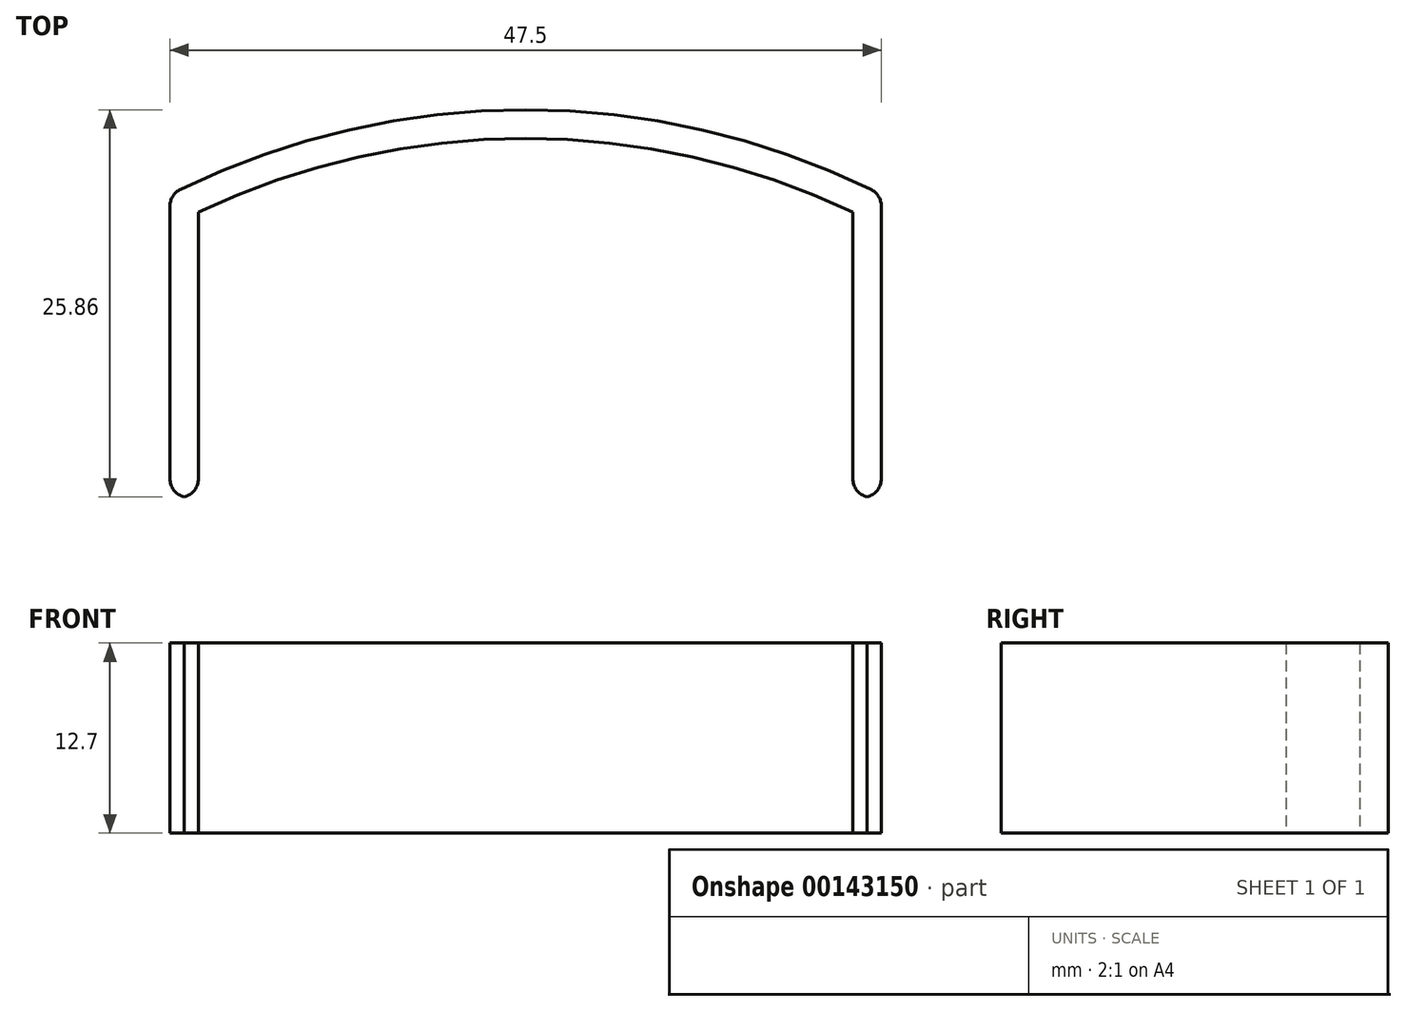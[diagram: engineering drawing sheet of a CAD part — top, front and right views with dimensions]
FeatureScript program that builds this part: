
annotation { "Feature Type Name" : "Feature", "Feature Type Description" : "" }
export const myFeature = defineFeature(function(context is Context, id is Id, definition is map)
    precondition{}
    {
        {
            var Q0;
            Q0=qCreatedBy(makeId("Top.planeOp"),FACE);
            var sketch = newSketch(context, id + "F0", { "sketchPlane" : qUnion([Q0])});
            skCircle(sketch, "E0", {"center": v(0, 0) * mm, "radius": 50.8 * mm});
            skCircle(sketch, "E1.0", {"center": v(0, 0) * mm, "radius": 52.7 * mm});
            skPoint(sketch, "E2", {"position": v(-21.84, 45.86) * mm});
            skPoint(sketch, "E3", {"position": v(-25.97, 45.86) * mm});
            skPoint(sketch, "E4", {"position": v(21.84, 45.86) * mm});
            skPoint(sketch, "E5", {"position": v(25.97, 45.86) * mm});
            skLineSegment(sketch, "E6", {"start": v(-25.97, 65.39) * mm, "end": v(-25.97, 26.81) * mm});
            skLineSegment(sketch, "E7", {"start": v(-21.84, 65.39) * mm, "end": v(-21.84, 26.81) * mm});
            skLineSegment(sketch, "E8", {"start": v(21.84, 65.39) * mm, "end": v(21.84, 26.81) * mm});
            skLineSegment(sketch, "E9", {"start": v(25.97, 65.39) * mm, "end": v(25.97, 26.81) * mm});
            skLineSegment(sketch, "E10", {"start": v(-25.97, 26.81) * mm, "end": v(-21.84, 26.81) * mm});
            skLineSegment(sketch, "E11", {"start": v(21.84, 26.81) * mm, "end": v(25.97, 26.81) * mm});
            skSolve(sketch);
        }
        {
            var Q0;
            {var subQ0=sQuery(id+"F0.wireOp",EDGE,"E7");var subQ1=sQuery(id+"F0.wireOp",EDGE,"E0");var subQ2=makeQuery(id+"F0.imprint","INTERSECT",VERTEX,{"derivedFrom":[subQ1,subQ0]});Q0=makeQuery(id+"F0.imprint","IMPRINT",FACE,{"disambiguationData":[TD([[makeQuery(id+"F0.imprint","IMPRINT",EDGE,{"disambiguationData":[TD([[subQ2,-1.0]])],"derivedFrom":subQ1}),-1.0]])]});}
            var Q1;
            {var subQ5=sQuery(id+"F0.wireOp",EDGE,"E10");Q1=makeQuery(id+"F0.imprint","IMPRINT",FACE,{"disambiguationData":[TD([[makeQuery(id+"F0.imprint","IMPRINT",EDGE,{"derivedFrom":subQ5}),1.0]])]});}
            var Q2;
            {var subQ0=sQuery(id+"F0.wireOp",EDGE,"E8");var subQ1=sQuery(id+"F0.wireOp",EDGE,"E0");var subQ2=makeQuery(id+"F0.imprint","INTERSECT",VERTEX,{"derivedFrom":[subQ1,subQ0]});Q2=makeQuery(id+"F0.imprint","IMPRINT",FACE,{"disambiguationData":[TD([[makeQuery(id+"F0.imprint","IMPRINT",EDGE,{"disambiguationData":[TD([[subQ2,1.0]])],"derivedFrom":subQ1}),-1.0]])]});}
            var Q3;
            {var subQ5=sQuery(id+"F0.wireOp",EDGE,"E11");Q3=makeQuery(id+"F0.imprint","IMPRINT",FACE,{"disambiguationData":[TD([[makeQuery(id+"F0.imprint","IMPRINT",EDGE,{"derivedFrom":subQ5}),1.0]])]});}
            var Q4;
            {var subQ0=sQuery(id+"F0.wireOp",EDGE,"E8");var subQ1=sQuery(id+"F0.wireOp",EDGE,"E0");var subQ2=makeQuery(id+"F0.imprint","INTERSECT",VERTEX,{"derivedFrom":[subQ1,subQ0]});Q4=makeQuery(id+"F0.imprint","IMPRINT",FACE,{"disambiguationData":[TD([[makeQuery(id+"F0.imprint","IMPRINT",EDGE,{"disambiguationData":[TD([[subQ2,-1.0]])],"derivedFrom":subQ1}),-1.0]])]});}
            extrude(context, id + "F1", {"entities" : qUnion([Q0, Q1, Q2, Q3, Q4]), "depth" : 12.7 * mm});
        }
        {
            var Q0;
            Q0=makeQuery(id+"F1.opExtrude","CAP_FACE",FACE,{"disambiguationData":[OSD([sQuery(id+"F0.wireOp",EDGE,"E0"),sQuery(id+"F0.wireOp",EDGE,"E1.0"),sQuery(id+"F0.wireOp",EDGE,"E6"),sQuery(id+"F0.wireOp",EDGE,"E7"),sQuery(id+"F0.wireOp",EDGE,"E8"),sQuery(id+"F0.wireOp",EDGE,"E9"),sQuery(id+"F0.wireOp",EDGE,"E10"),sQuery(id+"F0.wireOp",EDGE,"E11")])],"isStart":false});
            var sketch = newSketch(context, id + "F2", { "sketchPlane" : qUnion([Q0])});
            skLineSegment(sketch, "E12", {"start": v(-23.75, 52.28) * mm, "end": v(-23.75, 23.77) * mm});
            skLineSegment(sketch, "E13", {"start": v(0, 53.88) * mm, "end": v(0, 0) * mm, "construction": true});
            skPoint(sketch, "E13.startSnap0", {"position": v(0, 52.7) * mm});
            skLineSegment(sketch, "E14.MirrorCS", {"start": v(23.75, 52.28) * mm, "end": v(23.75, 23.77) * mm});
            skLineSegment(sketch, "E15", {"start": v(-23.75, 52.28) * mm, "end": v(-31.07, 52.14) * mm});
            skLineSegment(sketch, "E16", {"start": v(-31.07, 52.14) * mm, "end": v(-30.55, 23.77) * mm});
            skLineSegment(sketch, "E17", {"start": v(-30.55, 23.77) * mm, "end": v(-23.75, 23.77) * mm});
            skLineSegment(sketch, "E18.MirrorCS", {"start": v(23.75, 52.28) * mm, "end": v(31.07, 52.14) * mm});
            skLineSegment(sketch, "E19.MirrorCS", {"start": v(31.07, 52.14) * mm, "end": v(30.55, 23.77) * mm});
            skLineSegment(sketch, "E20.MirrorCS", {"start": v(30.55, 23.77) * mm, "end": v(23.75, 23.77) * mm});
            skSolve(sketch);
        }
        {
            var Q0;
            {var subQ0=sQuery(id+"F2.wireOp",EDGE,"E15");Q0=makeQuery(id+"F2.imprint","IMPRINT",FACE,{"disambiguationData":[TD([[makeQuery(id+"F2.imprint","IMPRINT",EDGE,{"derivedFrom":subQ0}),1.0]])]});}
            var Q1;
            {var subQ5=sQuery(id+"F2.wireOp",EDGE,"E18.MirrorCS");Q1=makeQuery(id+"F2.imprint","IMPRINT",FACE,{"disambiguationData":[TD([[makeQuery(id+"F2.imprint","IMPRINT",EDGE,{"derivedFrom":subQ5}),-1.0]])]});}
            var Q2;
            {var subQ5=makeQuery(id+"F1.opExtrude","CAP_EDGE",EDGE,{"disambiguationData":[OSD([sQuery(id+"F0.wireOp",EDGE,"E6")])],"isStart":false});Q2=makeQuery(id+"F2.imprint","IMPRINT",FACE,{"disambiguationData":[TD([[makeQuery(id+"F2.imprint","IMPRINT",EDGE,{"derivedFrom":subQ5}),1.0]])]});}
            var Q3;
            {var subQ5=makeQuery(id+"F1.opExtrude","CAP_EDGE",EDGE,{"disambiguationData":[OSD([sQuery(id+"F0.wireOp",EDGE,"E9")])],"isStart":false});Q3=makeQuery(id+"F2.imprint","IMPRINT",FACE,{"disambiguationData":[TD([[makeQuery(id+"F2.imprint","IMPRINT",EDGE,{"derivedFrom":subQ5}),-1.0]])]});}
            extrude(context, id + "F3", {"entities" : qUnion([Q0, Q1, Q2, Q3]), "operationType" : NewBodyOperationType.REMOVE, "endBound" : BoundingType.SYMMETRIC, "oppositeDirection" : true, "depth" : 64.39 * mm});
        }
        {
            var Q0;
            Q0=makeQuery(id+"F1.opExtrude","SWEPT_EDGE",EDGE,{"disambiguationData":[OSD([sQuery(id+"F0.wireOp",EDGE,"E7"),sQuery(id+"F0.wireOp",EDGE,"E10")])]});
            var Q1;
            Q1=makeQuery(id+"F3.boolean.opBoolean","INTERSECT",EDGE,{"derivedFrom":[makeQuery(id+"F1.opExtrude","SWEPT_FACE",FACE,{"disambiguationData":[OSD([sQuery(id+"F0.wireOp",EDGE,"E10")])]}),makeQuery(id+"F3.opExtrude","SWEPT_FACE",FACE,{"disambiguationData":[OSD([sQuery(id+"F2.wireOp",EDGE,"E12")])]})]});
            var Q2;
            Q2=makeQuery(id+"F1.opExtrude","SWEPT_EDGE",EDGE,{"disambiguationData":[OSD([sQuery(id+"F0.wireOp",EDGE,"E8"),sQuery(id+"F0.wireOp",EDGE,"E11")])]});
            var Q3;
            Q3=makeQuery(id+"F3.boolean.opBoolean","INTERSECT",EDGE,{"derivedFrom":[makeQuery(id+"F1.opExtrude","SWEPT_FACE",FACE,{"disambiguationData":[OSD([sQuery(id+"F0.wireOp",EDGE,"E11")])]}),makeQuery(id+"F3.opExtrude","SWEPT_FACE",FACE,{"disambiguationData":[OSD([sQuery(id+"F2.wireOp",EDGE,"E14.MirrorCS")])]})]});
            fillet(context, id + "F4", {"entities" : qUnion([Q0, Q1, Q2, Q3]), "radius" : 1.27 * mm, "tangentPropagation" : true, "allowEdgeOverflow" : false});
        }
        {
            var Q0;
            Q0=makeQuery(id+"F3.boolean.opBoolean","INTERSECT",EDGE,{"derivedFrom":[makeQuery(id+"F1.opExtrude","SWEPT_FACE",FACE,{"disambiguationData":[OSD([sQuery(id+"F0.wireOp",EDGE,"E1.0")])]}),makeQuery(id+"F3.opExtrude","SWEPT_FACE",FACE,{"disambiguationData":[OSD([sQuery(id+"F2.wireOp",EDGE,"E14.MirrorCS")])]})]});
            var Q1;
            Q1=makeQuery(id+"F3.boolean.opBoolean","INTERSECT",EDGE,{"derivedFrom":[makeQuery(id+"F1.opExtrude","SWEPT_FACE",FACE,{"disambiguationData":[OSD([sQuery(id+"F0.wireOp",EDGE,"E1.0")])]}),makeQuery(id+"F3.opExtrude","SWEPT_FACE",FACE,{"disambiguationData":[OSD([sQuery(id+"F2.wireOp",EDGE,"E12")])]})]});
            fillet(context, id + "F5", {"entities" : qUnion([Q0, Q1]), "radius" : 1.27 * mm, "tangentPropagation" : true, "allowEdgeOverflow" : false});
        }
    });
